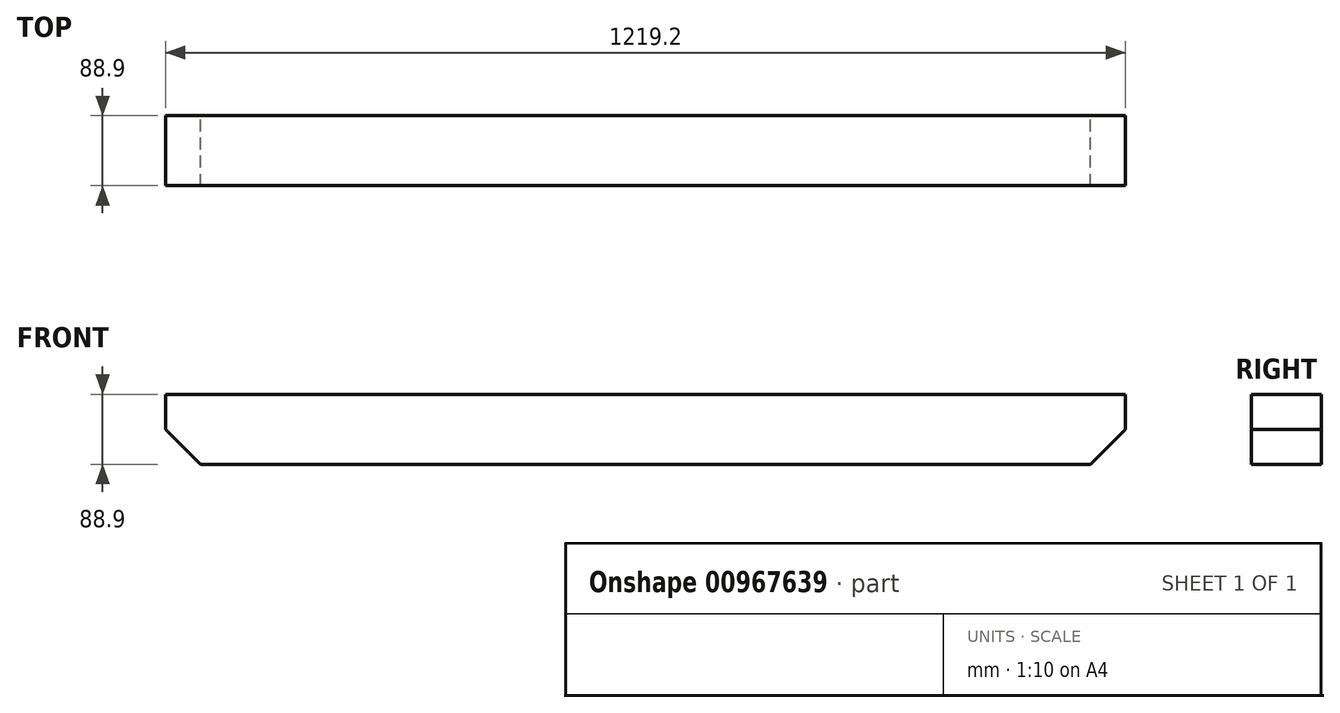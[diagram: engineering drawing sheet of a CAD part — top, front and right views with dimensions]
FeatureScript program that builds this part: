
annotation { "Feature Type Name" : "Feature", "Feature Type Description" : "" }
export const myFeature = defineFeature(function(context is Context, id is Id, definition is map)
    precondition{}
    {
        {
            var Q0;
            Q0=qCreatedBy(makeId("Front.planeOp"),FACE);
            var sketch = newSketch(context, id + "F0", { "sketchPlane" : qUnion([Q0])});
            skLineSegment(sketch, "E0.bottom", {"start": v(609.6, 44.45) * mm, "end": v(-609.6, 44.45) * mm});
            skLineSegment(sketch, "E0.top", {"start": v(609.6, -44.45) * mm, "end": v(-609.6, -44.45) * mm});
            skLineSegment(sketch, "E0.left", {"start": v(609.6, 44.45) * mm, "end": v(609.6, -44.45) * mm});
            skLineSegment(sketch, "E0.right", {"start": v(-609.6, 44.45) * mm, "end": v(-609.6, -44.45) * mm});
            skPoint(sketch, "E0.middle", {"position": v(0, 0) * mm});
            skLineSegment(sketch, "E1", {"start": v(609.6, 0) * mm, "end": v(565.15, -44.45) * mm});
            skLineSegment(sketch, "E2", {"start": v(-609.6, 0) * mm, "end": v(-565.15, -44.45) * mm});
            skSolve(sketch);
        }
        {
            var Q0;
            {var subQ1=sQuery(id+"F0.wireOp",EDGE,"E0.bottom");Q0=makeQuery(id+"F0.imprint","IMPRINT",FACE,{"disambiguationData":[TD([[makeQuery(id+"F0.imprint","IMPRINT",EDGE,{"derivedFrom":subQ1}),1.0]])]});}
            extrude(context, id + "F1", {"entities" : qUnion([Q0]), "depth" : 88.9 * mm, "offsetDistance" : 25.4 * mm});
        }
    });
